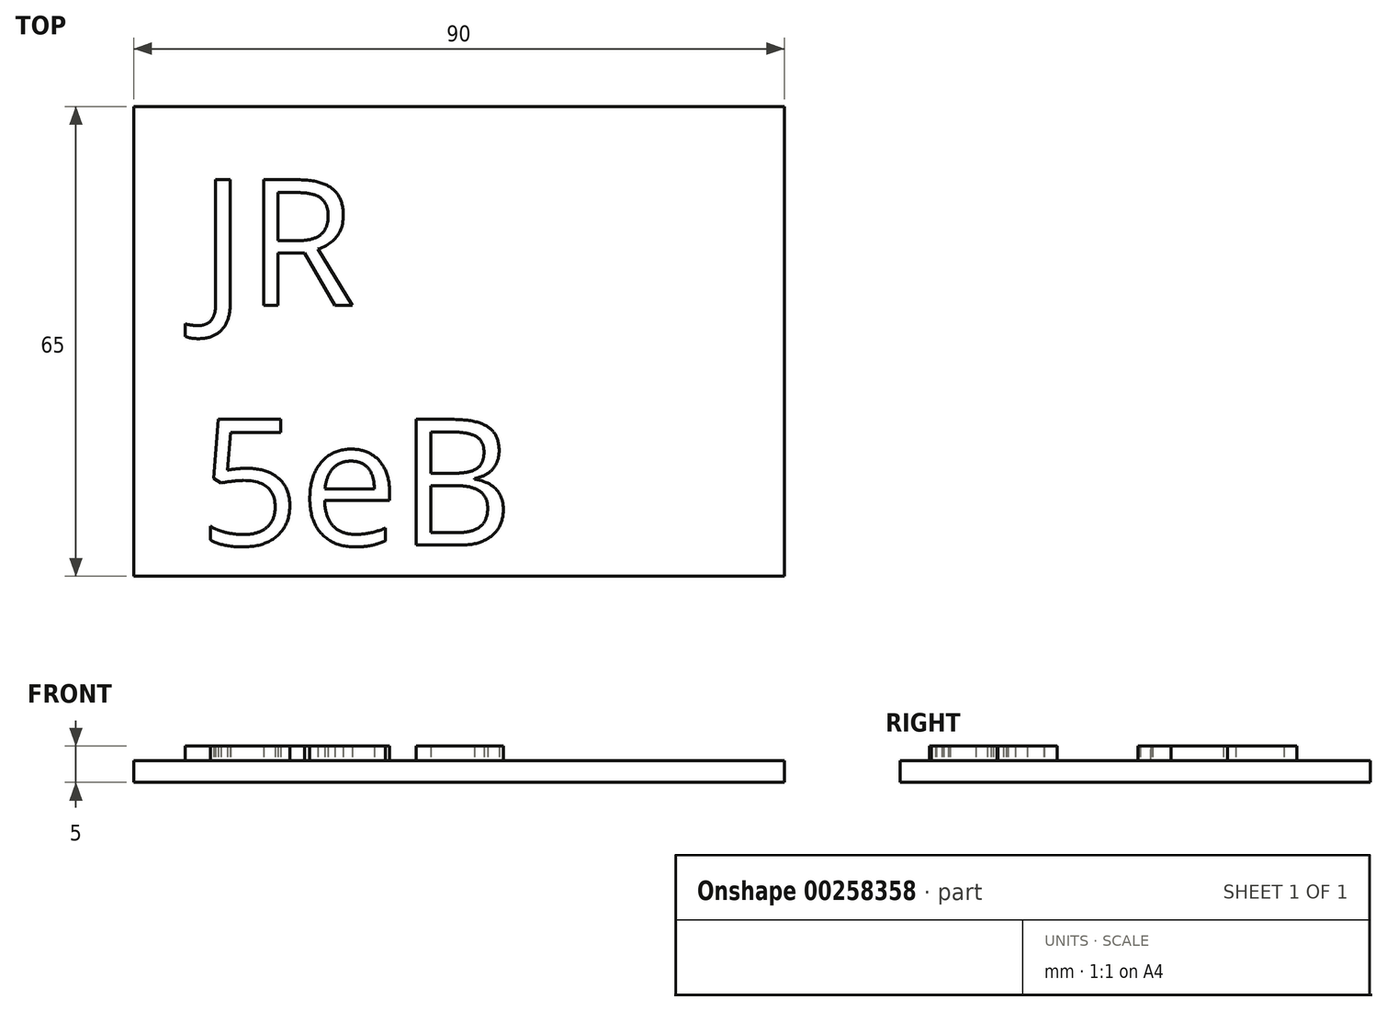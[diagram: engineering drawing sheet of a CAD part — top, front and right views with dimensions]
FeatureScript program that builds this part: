
annotation { "Feature Type Name" : "Feature", "Feature Type Description" : "" }
export const myFeature = defineFeature(function(context is Context, id is Id, definition is map)
    precondition{}
    {
        {
            var Q0;
            Q0=qCreatedBy(makeId("Top.planeOp"),FACE);
            var sketch = newSketch(context, id + "F0", { "sketchPlane" : qUnion([Q0])});
            skLineSegment(sketch, "E0.bottom", {"start": v(0, 0) * mm, "end": v(90, 0) * mm});
            skLineSegment(sketch, "E0.top", {"start": v(0, -65) * mm, "end": v(90, -65) * mm});
            skLineSegment(sketch, "E0.left", {"start": v(0, 0) * mm, "end": v(0, -65) * mm});
            skLineSegment(sketch, "E0.right", {"start": v(90, 0) * mm, "end": v(90, -65) * mm});
            skSolve(sketch);
        }
        {
            var Q0;
            Q0=makeQuery(id+"F0.imprint","IMPRINT",FACE,{"disambiguationData":[TD([[makeQuery(id+"F0.imprint","IMPRINT",EDGE,{"derivedFrom":sQuery(id+"F0.wireOp",EDGE,"E0.bottom")}),-1.0]])]});
            extrude(context, id + "F1", {"entities" : qUnion([Q0]), "depth" : 3 * mm});
        }
        {
            var Q0;
            Q0=makeQuery(id+"F1.opExtrude","CAP_FACE",FACE,{"disambiguationData":[OSD([sQuery(id+"F0.wireOp",EDGE,"E0.bottom"),sQuery(id+"F0.wireOp",EDGE,"E0.top"),sQuery(id+"F0.wireOp",EDGE,"E0.left"),sQuery(id+"F0.wireOp",EDGE,"E0.right")])],"isStart":false});
            var sketch = newSketch(context, id + "F2", { "sketchPlane" : qUnion([Q0])});
            skText(sketch, "E1", { "text": "JR\n5eB", "fontName": "OpenSans-Regular.ttf"});
            const initialGuessF2  = {"E1": [0.00906, -0.02754, 1, 0, 0.01755]};
            skSetInitialGuess(sketch, initialGuessF2);
            skSolve(sketch);
        }
        {
            var Q0;
            Q0 = qSketchRegion(id + "F2", true);
            extrude(context, id + "F3", {"entities" : qUnion([Q0]), "operationType" : NewBodyOperationType.ADD, "depth" : 2 * mm});
        }
    });
